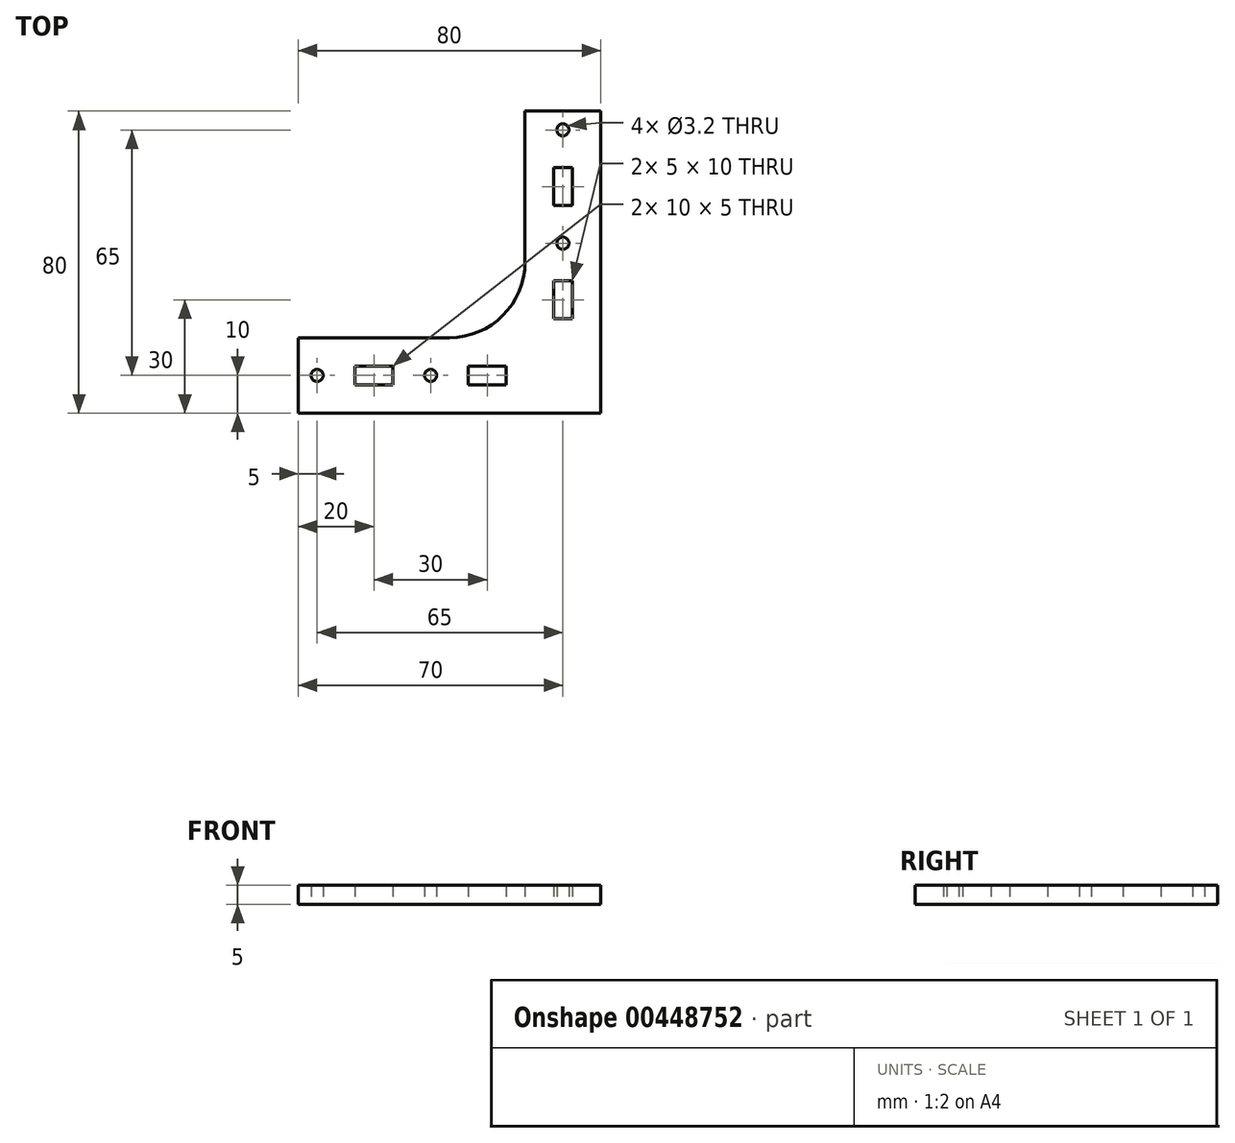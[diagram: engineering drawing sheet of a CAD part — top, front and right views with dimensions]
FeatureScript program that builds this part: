
annotation { "Feature Type Name" : "Feature", "Feature Type Description" : "" }
export const myFeature = defineFeature(function(context is Context, id is Id, definition is map)
    precondition{}
    {
        {
            assignVariable(context, id + "F0", {"name" : "thickness", "anyValue" : 5 * mm});
        }
        {
            var Q0;
            Q0=qCreatedBy(makeId("Top.planeOp"),FACE);
            var sketch = newSketch(context, id + "F1", { "sketchPlane" : qUnion([Q0])});
            skLineSegment(sketch, "E0", {"start": v(0, 0) * mm, "end": v(-80, 0) * mm});
            skLineSegment(sketch, "E1", {"start": v(-70, 0) * mm, "end": v(-70, 20) * mm, "construction": true});
            skLineSegment(sketch, "E2", {"start": v(-80, 20) * mm, "end": v(-40, 20) * mm});
            skLineSegment(sketch, "E3", {"start": v(-20, 40) * mm, "end": v(-20, 80) * mm});
            skLineSegment(sketch, "E4", {"start": v(-20, 70) * mm, "end": v(0, 70) * mm, "construction": true});
            skLineSegment(sketch, "E5", {"start": v(0, 80) * mm, "end": v(0, 0) * mm});
            skLineSegment(sketch, "E6", {"start": v(-70, 10) * mm, "end": v(-10, 10) * mm, "construction": true});
            skLineSegment(sketch, "E7", {"start": v(-10, 70) * mm, "end": v(-10, 10) * mm, "construction": true});
            skLineSegment(sketch, "E8.bottom", {"start": v(-55, 12.5) * mm, "end": v(-65, 12.5) * mm});
            skLineSegment(sketch, "E8.top", {"start": v(-55, 7.5) * mm, "end": v(-65, 7.5) * mm});
            skLineSegment(sketch, "E8.left", {"start": v(-55, 12.5) * mm, "end": v(-55, 7.5) * mm});
            skLineSegment(sketch, "E8.right", {"start": v(-65, 12.5) * mm, "end": v(-65, 7.5) * mm});
            skPoint(sketch, "E8.middle", {"position": v(-60, 10) * mm});
            skLineSegment(sketch, "E9.bottom", {"start": v(-25, 12.5) * mm, "end": v(-35, 12.5) * mm});
            skLineSegment(sketch, "E9.top", {"start": v(-25, 7.5) * mm, "end": v(-35, 7.5) * mm});
            skLineSegment(sketch, "E9.left", {"start": v(-25, 12.5) * mm, "end": v(-25, 7.5) * mm});
            skLineSegment(sketch, "E9.right", {"start": v(-35, 12.5) * mm, "end": v(-35, 7.5) * mm});
            skPoint(sketch, "E9.middle", {"position": v(-30, 10) * mm});
            skLineSegment(sketch, "E10.bottom", {"start": v(-7.5, 35) * mm, "end": v(-12.5, 35) * mm});
            skLineSegment(sketch, "E10.top", {"start": v(-7.5, 25) * mm, "end": v(-12.5, 25) * mm});
            skLineSegment(sketch, "E10.left", {"start": v(-7.5, 35) * mm, "end": v(-7.5, 25) * mm});
            skLineSegment(sketch, "E10.right", {"start": v(-12.5, 35) * mm, "end": v(-12.5, 25) * mm});
            skPoint(sketch, "E10.middle", {"position": v(-10, 30) * mm});
            skLineSegment(sketch, "E11.bottom", {"start": v(-7.5, 65) * mm, "end": v(-12.5, 65) * mm});
            skLineSegment(sketch, "E11.top", {"start": v(-7.5, 55) * mm, "end": v(-12.5, 55) * mm});
            skLineSegment(sketch, "E11.left", {"start": v(-7.5, 65) * mm, "end": v(-7.5, 55) * mm});
            skLineSegment(sketch, "E11.right", {"start": v(-12.5, 65) * mm, "end": v(-12.5, 55) * mm});
            skPoint(sketch, "E11.middle", {"position": v(-10, 60) * mm});
            skCircle(sketch, "E12", {"center": v(-45, 10) * mm, "radius": 1.6 * mm});
            skCircle(sketch, "E13", {"center": v(-10, 45) * mm, "radius": 1.6 * mm});
            skPoint(sketch, "E14.visualSharp", {"position": v(-20, 20) * mm});
            skArc(sketch, "E14.filletArc", {"start": v(-40, 20) * mm, "mid": v(-25.86, 25.86) * mm, "end": v(-20, 40) * mm});
            skPoint(sketch, "E15.visualSharp", {"position": v(-70, 20) * mm});
            skPoint(sketch, "E16.visualSharp", {"position": v(-70, 0) * mm});
            skPoint(sketch, "E17.visualSharp", {"position": v(-20, 70) * mm});
            skPoint(sketch, "E18.visualSharp", {"position": v(0, 70) * mm});
            skLineSegment(sketch, "E19", {"start": v(-80, 20) * mm, "end": v(-80, 0) * mm});
            skCircle(sketch, "E20", {"center": v(-75, 10) * mm, "radius": 1.6 * mm});
            skPoint(sketch, "E20.centerSnap0", {"position": v(-80, 10) * mm});
            skLineSegment(sketch, "E21", {"start": v(0, 80) * mm, "end": v(-20, 80) * mm});
            skCircle(sketch, "E22", {"center": v(-10, 75) * mm, "radius": 1.6 * mm});
            skPoint(sketch, "E22.centerSnap0", {"position": v(-10, 80) * mm});
            skSolve(sketch);
        }
        {
            var Q0;
            Q0=qSketchRegion(id+"F1",true);
            extrude(context, id + "F2", {"entities" : qUnion([Q0]), "depth" : getVariable(context, 'thickness')});
        }
    });
